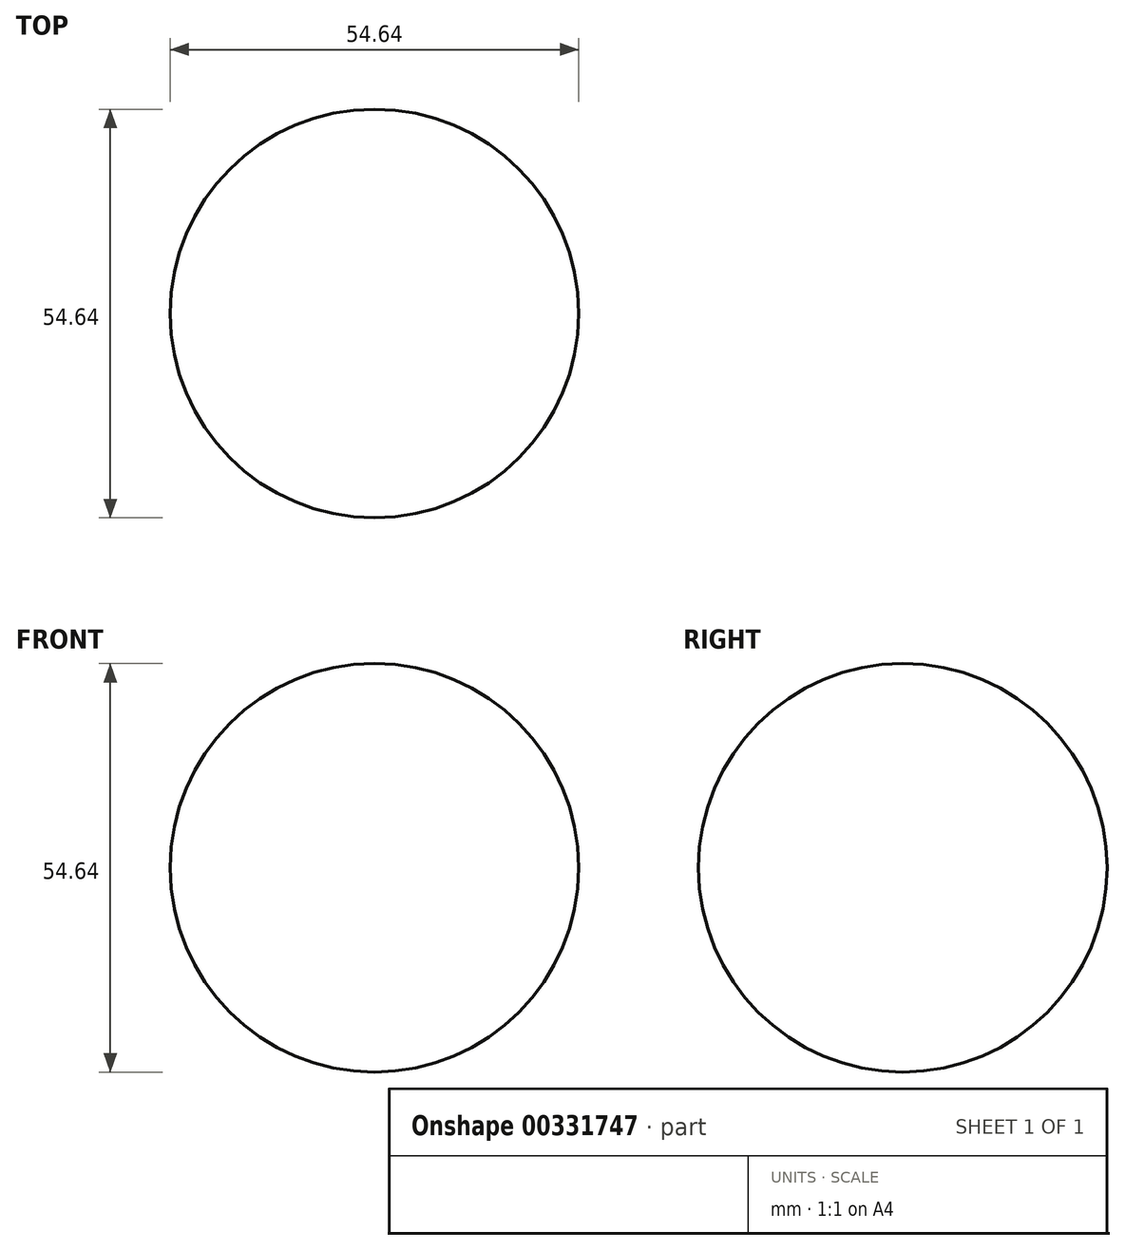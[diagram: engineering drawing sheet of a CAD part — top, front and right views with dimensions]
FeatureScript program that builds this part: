
annotation { "Feature Type Name" : "Feature", "Feature Type Description" : "" }
export const myFeature = defineFeature(function(context is Context, id is Id, definition is map)
    precondition{}
    {
        {
            var Q0;
            Q0=qCreatedBy(makeId("Right.planeOp"),FACE);
            var sketch = newSketch(context, id + "F0", { "sketchPlane" : qUnion([Q0])});
            skArc(sketch, "E0", {"start": v(0, 27.32) * mm, "mid": v(-27.32, 0) * mm, "end": v(0, -27.32) * mm});
            skLineSegment(sketch, "E1", {"start": v(0, 27.32) * mm, "end": v(0, -27.32) * mm});
            skSolve(sketch);
        }
        {
            var Q0;
            Q0=qCreatedBy(makeId("Right.planeOp"),FACE);
            var sketch = newSketch(context, id + "F1", { "sketchPlane" : qUnion([Q0])});
            skLineSegment(sketch, "E2", {"start": v(0, 0) * mm, "end": v(0, 77.68) * mm});
            skSolve(sketch);
        }
        {
            var Q0;
            Q0=makeQuery(id+"F0.imprint","IMPRINT",FACE,{"disambiguationData":[TD([[makeQuery(id+"F0.imprint","IMPRINT",EDGE,{"derivedFrom":sQuery(id+"F0.wireOp",EDGE,"E0")}),1.0]])]});
            var Q1;
            Q1=sQuery(id+"F1.wireOp",EDGE,"E2");
            revolve(context, id + "F2", {"entities" : qUnion([Q0]), "axis" : qUnion([Q1]), "revolveType" : RevolveType.FULL});
        }
    });
